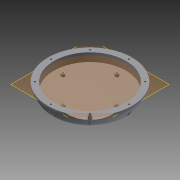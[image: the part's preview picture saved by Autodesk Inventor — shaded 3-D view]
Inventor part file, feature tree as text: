
AUTODESK INVENTOR PART (.ipt)
format: ipt  version: 2014 (Build 180170000, 170)  size: 272,896 bytes
history: native  units: mm
features: sketch x7, projected_geometry x7, extrude x5, fillet x2, plane x1, loft x1
ambient origin geometry x8: Origin, YZ Plane, XZ Plane, XY Plane, X Axis, Y Axis, Z Axis, Center Point
bodies: Solid1 (feature_tree)
feature tree (23):
  sketch  "Sketch1"  dims[d0=120.0mm d1=20.0mm d2=140.0mm]
  plane  "Work Plane1"
  loft  "Loft1"
  fillet  "Fillet1"  Radius=140.0mm
  extrude  "Extrusion1"  TaperAngle=0.0deg  [1 undecoded]
  extrude  "Extrusion2"  Depth=120.0mm
  extrude  "Extrusion3"  Depth=10.0mm
  fillet  "Fillet2"  Radius=5.5mm
  extrude  "Extrusion4"  Depth=5.5mm
  extrude  "Extrusion5"  TaperAngle=45.0deg  [1 undecoded]
  sketch  "Sketch2"  dims[d3=0.0mm d4=90.0deg d5=0.0mm d6=90.0deg]
  sketch  "Sketch3"  dims[d7=20.0mm d8=120.0mm]
  sketch  "Sketch4"  dims[d9=10.0mm d10=0.0mm d11=130.0mm d12=5.5mm]
  sketch  "Sketch5"  dims[d13=5.5mm d14=5.5mm]
  sketch  "Sketch6"  dims[d15=5.5mm d16=45.0deg]
  projected_geometry  "Projected Loop1"
  projected_geometry  "Projected Loop2"
  projected_geometry  "Projected Loop3"
  projected_geometry  "Projected Loop4"
  projected_geometry  "Projected Loop5"
  projected_geometry  "Projected Loop6"
  projected_geometry  "Projected Loop7"
  sketch  "Sketch7"  dims[d17=5.5mm d18=5.5mm d19=5.5mm d20=5.5mm d21=10.0mm d22=0.0mm d23=4.0mm d24=0.0mm d25=20.0mm d26=3.0mm d27=3.0mm d28=3.0mm d29=3.0mm d30=3.0mm d31=3.0mm d32=3.0mm d33=3.0mm d34=4.0mm d35=0.0mm d36=90.0mm d37=6.0mm d38=2.5mm d39=6.0mm d40=2.5mm d41=6.0mm d42=2.5mm d43=6.0mm d44=2.5mm d45=4.0mm d46=0.0mm]
note: 2 required parameter values undecoded (feature->parameter linkage not recoverable at this tier; creation-order binding heuristic only, values carry confidence <= 0.55)
